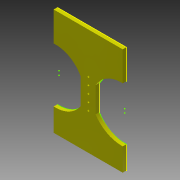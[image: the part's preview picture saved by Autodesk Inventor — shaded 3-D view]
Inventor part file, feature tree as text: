
AUTODESK INVENTOR PART (.ipt)
format: ipt  version: 2013 (Build 170138000, 138)  size: 276,480 bytes
history: native  units: mm
features: sketch x11, extrude x9, other x1, hole x1
ambient origin geometry x8: Origin, YZ Plane, XZ Plane, XY Plane, X Axis, Y Axis, Z Axis, Center Point
feature tree (22):
  other  "ソリッド1"
  extrude  "押し出し1"  Depth=25.0mm
  sketch  "スケッチ2"
  extrude  "押し出し3"  Depth=79.965mm
  extrude  "押し出し4"  Depth=34.641mm
  extrude  "押し出し5"  Depth=90.0mm
  extrude  "押し出し6"  Depth=94.0mm
  extrude  "押し出し7"  Depth=31.0mm
  extrude  "押し出し8"  Depth=94.0mm
  extrude  "押し出し9"  Depth=40.0mm
  extrude  "押し出し10"  Depth=90.0mm
  hole  "穴1"  [1 undecoded]
  sketch  "スケッチ1"
  sketch  "スケッチ3"
  sketch  "スケッチ4"
  sketch  "スケッチ5"
  sketch  "スケッチ6"
  sketch  "スケッチ7"
  sketch  "スケッチ8"
  sketch  "スケッチ9"
  sketch  "スケッチ10"
  sketch  "スケッチ11"
note: 1 required parameter value undecoded (feature->parameter linkage not recoverable at this tier; creation-order binding heuristic only, values carry confidence <= 0.55)
